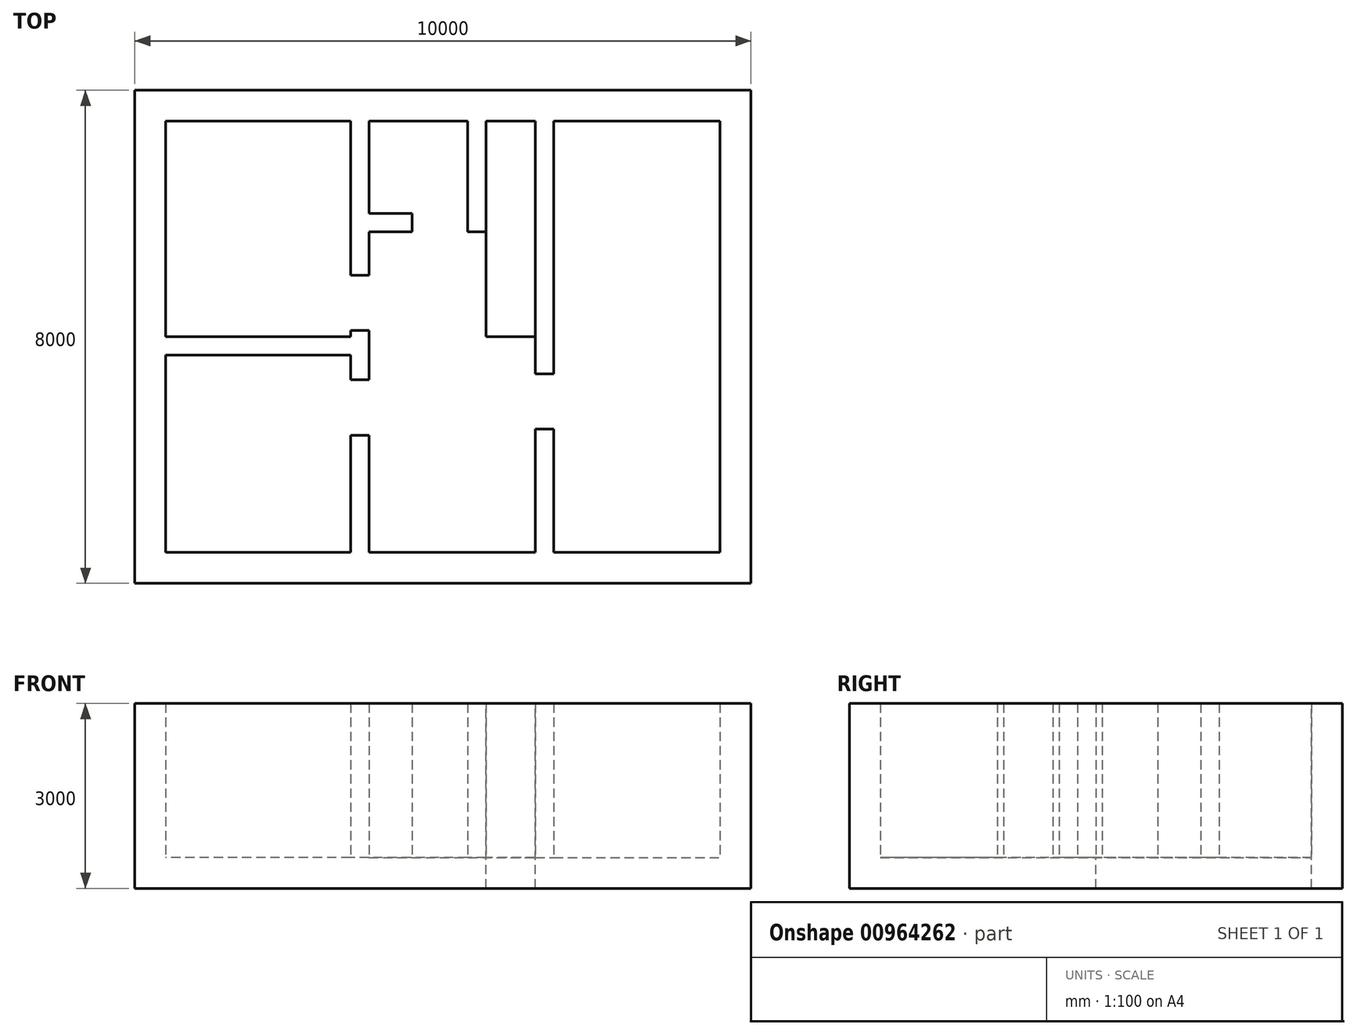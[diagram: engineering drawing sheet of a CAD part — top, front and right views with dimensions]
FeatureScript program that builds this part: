
annotation { "Feature Type Name" : "Feature", "Feature Type Description" : "" }
export const myFeature = defineFeature(function(context is Context, id is Id, definition is map)
    precondition{}
    {
        {
            var Q0;
            Q0=qCreatedBy(makeId("Top.planeOp"),FACE);
            var sketch = newSketch(context, id + "F0", { "sketchPlane" : qUnion([Q0])});
            skLineSegment(sketch, "E0.bottom", {"start": v(5000, 4000) * mm, "end": v(-5000, 4000) * mm});
            skLineSegment(sketch, "E0.right", {"start": v(-5000, 4000) * mm, "end": v(-5000, -4000) * mm});
            skPoint(sketch, "E0.middle", {"position": v(0, 0) * mm});
            skLineSegment(sketch, "E1.right", {"start": v(5000, -4000) * mm, "end": v(5000, 4000) * mm});
            skLineSegment(sketch, "E2", {"start": v(-5000, -4000) * mm, "end": v(5000, -4000) * mm});
            skSolve(sketch);
        }
        {
            var Q0;
            Q0 = qSketchRegion(id + "F0", true);
            extrude(context, id + "F1", {"entities" : qUnion([Q0]), "depth" : 3000 * mm, "offsetDistance" : 25 * mm});
        }
        {
            var Q0;
            Q0=makeQuery(id+"F1.opExtrude","CAP_FACE",FACE,{"disambiguationData":[OSD([sQuery(id+"F0.wireOp",EDGE,"E0.bottom"),sQuery(id+"F0.wireOp",EDGE,"E0.top"),sQuery(id+"F0.wireOp",EDGE,"E0.left"),sQuery(id+"F0.wireOp",EDGE,"E0.right")])],"isStart":false});
            shell(context, id + "F2", {"entities" : qUnion([Q0]), "thickness" : 500 * mm});
        }
        {
            var Q0;
            Q0=makeQuery(id+"F2.opShell","OFFSET_FACE",FACE,{"disambiguationData":[OSD([sQuery(id+"F0.wireOp",EDGE,"E0.bottom"),sQuery(id+"F0.wireOp",EDGE,"E0.right"),sQuery(id+"F0.wireOp",EDGE,"E1.right"),sQuery(id+"F0.wireOp",EDGE,"E2")])]});
            var sketch = newSketch(context, id + "F3", { "sketchPlane" : qUnion([Q0])});
            skLineSegment(sketch, "E3.bottom", {"start": v(1500, 3500) * mm, "end": v(700, 3500) * mm});
            skLineSegment(sketch, "E3.top", {"start": v(1500, 0) * mm, "end": v(700, 0) * mm});
            skLineSegment(sketch, "E3.left", {"start": v(1500, 3500) * mm, "end": v(1500, 0) * mm});
            skLineSegment(sketch, "E3.right", {"start": v(700, 3500) * mm, "end": v(700, 0) * mm});
            skSolve(sketch);
        }
        {
            var Q0;
            Q0=makeQuery(id+"F3.imprint","IMPRINT",FACE,{"disambiguationData":[TD([[makeQuery(id+"F3.imprint","IMPRINT",EDGE,{"derivedFrom":sQuery(id+"F3.wireOp",EDGE,"E3.bottom")}),1.0]])]});
            extrude(context, id + "F4", {"entities" : qUnion([Q0]), "operationType" : NewBodyOperationType.REMOVE, "endBound" : BoundingType.THROUGH_ALL, "oppositeDirection" : true, "depth" : 25 * mm, "offsetDistance" : 25 * mm});
        }
        {
            var Q0;
            Q0=makeQuery(id+"F2.opShell","OFFSET_FACE",FACE,{"disambiguationData":[OSD([sQuery(id+"F0.wireOp",EDGE,"E0.bottom"),sQuery(id+"F0.wireOp",EDGE,"E0.right"),sQuery(id+"F0.wireOp",EDGE,"E1.right"),sQuery(id+"F0.wireOp",EDGE,"E2")])]});
            var sketch = newSketch(context, id + "F5", { "sketchPlane" : qUnion([Q0])});
            skLineSegment(sketch, "E4.bottom", {"start": v(-1200, 3500) * mm, "end": v(-1500, 3500) * mm});
            skLineSegment(sketch, "E4.top", {"start": v(-1200, 1000) * mm, "end": v(-1500, 1000) * mm});
            skLineSegment(sketch, "E4.left", {"start": v(-1200, 3500) * mm, "end": v(-1200, 2000) * mm});
            skLineSegment(sketch, "E4.right", {"start": v(-1500, 3500) * mm, "end": v(-1500, 1000) * mm});
            skLineSegment(sketch, "E5.bottom", {"start": v(-1500, 100) * mm, "end": v(-1200, 100) * mm});
            skLineSegment(sketch, "E5.top", {"start": v(-1500, -700) * mm, "end": v(-1200, -700) * mm});
            skLineSegment(sketch, "E5.left", {"start": v(-1500, 100) * mm, "end": v(-1500, 0) * mm});
            skLineSegment(sketch, "E5.right", {"start": v(-1200, 100) * mm, "end": v(-1200, -700) * mm});
            skPoint(sketch, "E6.oppositeSnap0", {"position": v(-1500, -300) * mm});
            skLineSegment(sketch, "E6.bottom", {"start": v(-1500, 0) * mm, "end": v(-4500, 0) * mm});
            skLineSegment(sketch, "E6.top", {"start": v(-1500, -300) * mm, "end": v(-4500, -300) * mm});
            skLineSegment(sketch, "E6.right", {"start": v(-4500, 0) * mm, "end": v(-4500, -300) * mm});
            skLineSegment(sketch, "E7.trimOffspring", {"start": v(-1500, -300) * mm, "end": v(-1500, -700) * mm});
            skLineSegment(sketch, "E8.bottom", {"start": v(-1500, -1600) * mm, "end": v(-1200, -1600) * mm});
            skLineSegment(sketch, "E8.top", {"start": v(-1500, -3500) * mm, "end": v(-1200, -3500) * mm});
            skLineSegment(sketch, "E8.left", {"start": v(-1500, -1600) * mm, "end": v(-1500, -3500) * mm});
            skLineSegment(sketch, "E8.right", {"start": v(-1200, -1600) * mm, "end": v(-1200, -3500) * mm});
            skLineSegment(sketch, "E9", {"start": v(1500, -3500) * mm, "end": v(1500, -1500) * mm});
            skLineSegment(sketch, "E10", {"start": v(1800, 3500) * mm, "end": v(1800, -600) * mm});
            skLineSegment(sketch, "E11", {"start": v(1800, -3500) * mm, "end": v(1500, -3500) * mm});
            skLineSegment(sketch, "E12", {"start": v(1800, 3500) * mm, "end": v(1500, 3500) * mm});
            skLineSegment(sketch, "E13", {"start": v(1500, -600) * mm, "end": v(1800, -600) * mm});
            skLineSegment(sketch, "E14", {"start": v(1500, -1500) * mm, "end": v(1800, -1500) * mm});
            skLineSegment(sketch, "E15.trimOffspring", {"start": v(1500, -600) * mm, "end": v(1500, 3500) * mm});
            skLineSegment(sketch, "E16.trimOffspring", {"start": v(1800, -1500) * mm, "end": v(1800, -3500) * mm});
            skLineSegment(sketch, "E17.bottom", {"start": v(700, 3500) * mm, "end": v(400, 3500) * mm});
            skLineSegment(sketch, "E17.top", {"start": v(700, 1700) * mm, "end": v(400, 1700) * mm});
            skLineSegment(sketch, "E17.left", {"start": v(700, 3500) * mm, "end": v(700, 1700) * mm});
            skLineSegment(sketch, "E17.right", {"start": v(400, 3500) * mm, "end": v(400, 1700) * mm});
            skLineSegment(sketch, "E18.trimOffspring", {"start": v(-1200, 1700) * mm, "end": v(-1200, 1000) * mm});
            skLineSegment(sketch, "E19", {"start": v(-1200, 2000) * mm, "end": v(-500, 2000) * mm});
            skLineSegment(sketch, "E20", {"start": v(-500, 2000) * mm, "end": v(-500, 1700) * mm});
            skLineSegment(sketch, "E21", {"start": v(-500, 1700) * mm, "end": v(-1200, 1700) * mm});
            skSolve(sketch);
        }
        {
            var Q0;
            Q0 = qSketchRegion(id + "F5", true);
            var Q1;
            Q1=makeQuery(id+"F1.opExtrude","CAP_FACE",FACE,{"disambiguationData":[OSD([sQuery(id+"F0.wireOp",EDGE,"E0.bottom"),sQuery(id+"F0.wireOp",EDGE,"E0.top"),sQuery(id+"F0.wireOp",EDGE,"E0.left"),sQuery(id+"F0.wireOp",EDGE,"E0.right")])],"isStart":false});
            extrude(context, id + "F6", {"entities" : qUnion([Q0]), "operationType" : NewBodyOperationType.ADD, "endBound" : BoundingType.UP_TO_SURFACE, "depth" : 25 * mm, "endBoundEntityFace" : qUnion([Q1]), "offsetDistance" : 25 * mm});
        }
    });
